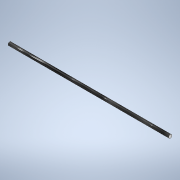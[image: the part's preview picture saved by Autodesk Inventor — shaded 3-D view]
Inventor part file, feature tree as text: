
AUTODESK INVENTOR PART (.ipt)
format: ipt  version: 2021 (Build 250183000, 183)  size: 101,888 bytes
history: native  units: in
note: dims shown in document units (in); Inventor stores cm internally (conversion verified against a paired STEP export)
features: extrude x1, sketch x1
ambient origin geometry x8: Origin, YZ Plane, XZ Plane, XY Plane, X Axis, Y Axis, Z Axis, Center Point
bodies: Solid1 (feature_tree)
feature tree (2):
  extrude  "Extrusion1"  Depth=0.2524in TaperAngle=0.0deg
  sketch  "Sketch1"  dims[d0=0.0053in d1=0.2524in d2=0.0in]
